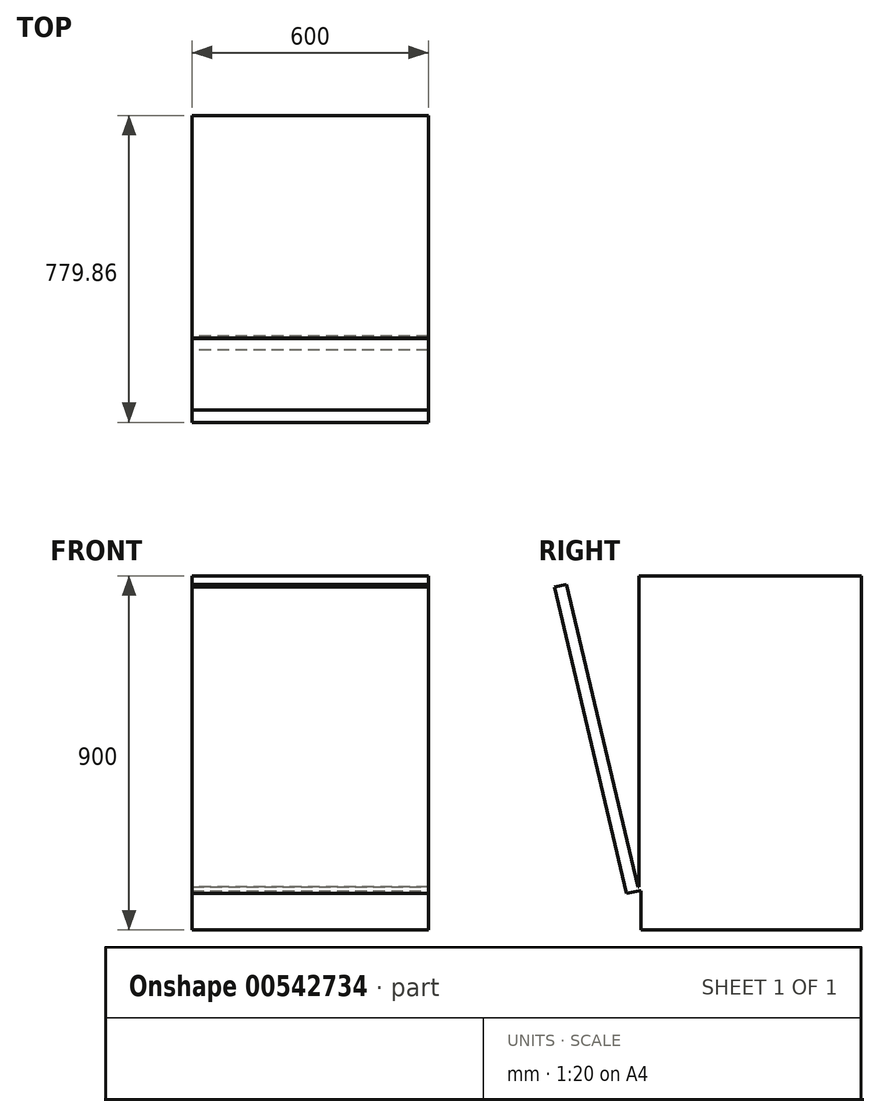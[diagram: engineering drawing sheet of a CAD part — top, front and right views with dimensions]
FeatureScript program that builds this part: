
annotation { "Feature Type Name" : "Feature", "Feature Type Description" : "" }
export const myFeature = defineFeature(function(context is Context, id is Id, definition is map)
    precondition{}
    {
        {
            var Q0;
            Q0=qCreatedBy(makeId("Top.planeOp"),FACE);
            var sketch = newSketch(context, id + "F0", { "sketchPlane" : qUnion([Q0])});
            skLineSegment(sketch, "E0.bottom", {"start": v(300, 300) * mm, "end": v(-300, 300) * mm});
            skLineSegment(sketch, "E0.top", {"start": v(300, -300) * mm, "end": v(-300, -300) * mm});
            skLineSegment(sketch, "E0.left", {"start": v(300, 300) * mm, "end": v(300, -300) * mm});
            skLineSegment(sketch, "E0.right", {"start": v(-300, 300) * mm, "end": v(-300, -300) * mm});
            skPoint(sketch, "E0.middle", {"position": v(0, 0) * mm});
            skSolve(sketch);
        }
        {
            var Q0;
            Q0=qSketchRegion(id+"F0",true);
            extrude(context, id + "F1", {"entities" : qUnion([Q0]), "depth" : 900 * mm, "offsetDistance" : 25 * mm});
        }
        {
            var Q0;
            Q0=makeQuery(id+"F1.opExtrude","SWEPT_FACE",FACE,{"disambiguationData":[OSD([sQuery(id+"F0.wireOp",EDGE,"E0.top")])]});
            var sketch = newSketch(context, id + "F2", { "sketchPlane" : qUnion([Q0])});
            skLineSegment(sketch, "E1.bottom", {"start": v(-300, 0) * mm, "end": v(300, 0) * mm});
            skLineSegment(sketch, "E1.top", {"start": v(-300, 100) * mm, "end": v(300, 100) * mm});
            skLineSegment(sketch, "E1.left", {"start": v(-300, 0) * mm, "end": v(-300, 100) * mm});
            skLineSegment(sketch, "E1.right", {"start": v(300, 0) * mm, "end": v(300, 100) * mm});
            skSolve(sketch);
        }
        {
            var Q0;
            Q0=qSketchRegion(id+"F2",true);
            extrude(context, id + "F3", {"entities" : qUnion([Q0]), "operationType" : NewBodyOperationType.REMOVE, "oppositeDirection" : true, "depth" : 40 * mm, "offsetDistance" : 25 * mm});
        }
        {
            var Q0;
            Q0=makeQuery(id+"F1.opExtrude","SWEPT_FACE",FACE,{"disambiguationData":[OSD([sQuery(id+"F0.wireOp",EDGE,"E0.top")])]});
            var sketch = newSketch(context, id + "F4", { "sketchPlane" : qUnion([Q0])});
            skLineSegment(sketch, "E2.bottom", {"start": v(-300, 900) * mm, "end": v(300, 900) * mm});
            skLineSegment(sketch, "E2.top", {"start": v(-300, 100) * mm, "end": v(300, 100) * mm});
            skLineSegment(sketch, "E2.left", {"start": v(-300, 900) * mm, "end": v(-300, 100) * mm});
            skLineSegment(sketch, "E2.right", {"start": v(300, 900) * mm, "end": v(300, 100) * mm});
            skSolve(sketch);
        }
        {
            var Q0;
            Q0 = qSketchRegion(id + "F4", true);
            extrude(context, id + "F5", {"entities" : qUnion([Q0]), "operationType" : NewBodyOperationType.REMOVE, "oppositeDirection" : true, "depth" : 35 * mm, "offsetDistance" : 25 * mm});
        }
        {
            var Q0;
            Q0=qCreatedBy(makeId("Right.planeOp"),FACE);
            var sketch = newSketch(context, id + "F6", { "sketchPlane" : qUnion([Q0])});
            skLineSegment(sketch, "E3", {"start": v(-265, 100) * mm, "end": v(-296.14, 92.65) * mm});
            skLineSegment(sketch, "E4", {"start": v(-296.14, 92.65) * mm, "end": v(-479.86, 871.27) * mm});
            skLineSegment(sketch, "E5", {"start": v(-479.86, 871.27) * mm, "end": v(-448.71, 878.62) * mm});
            skLineSegment(sketch, "E6", {"start": v(-448.71, 878.62) * mm, "end": v(-267.3, 109.73) * mm});
            skLineSegment(sketch, "E7", {"start": v(-265, 100) * mm, "end": v(-255.27, 102.3) * mm});
            skLineSegment(sketch, "E8", {"start": v(-255.27, 102.3) * mm, "end": v(-257.56, 112.03) * mm});
            skLineSegment(sketch, "E9", {"start": v(-257.56, 112.03) * mm, "end": v(-267.3, 109.73) * mm});
            skSolve(sketch);
        }
        {
            var Q0;
            Q0 = qSketchRegion(id + "F6", true);
            extrude(context, id + "F7", {"entities" : qUnion([Q0]), "operationType" : NewBodyOperationType.ADD, "depth" : 600 * mm, "offsetDistance" : 25 * mm, "symmetric" : true});
        }
    });
